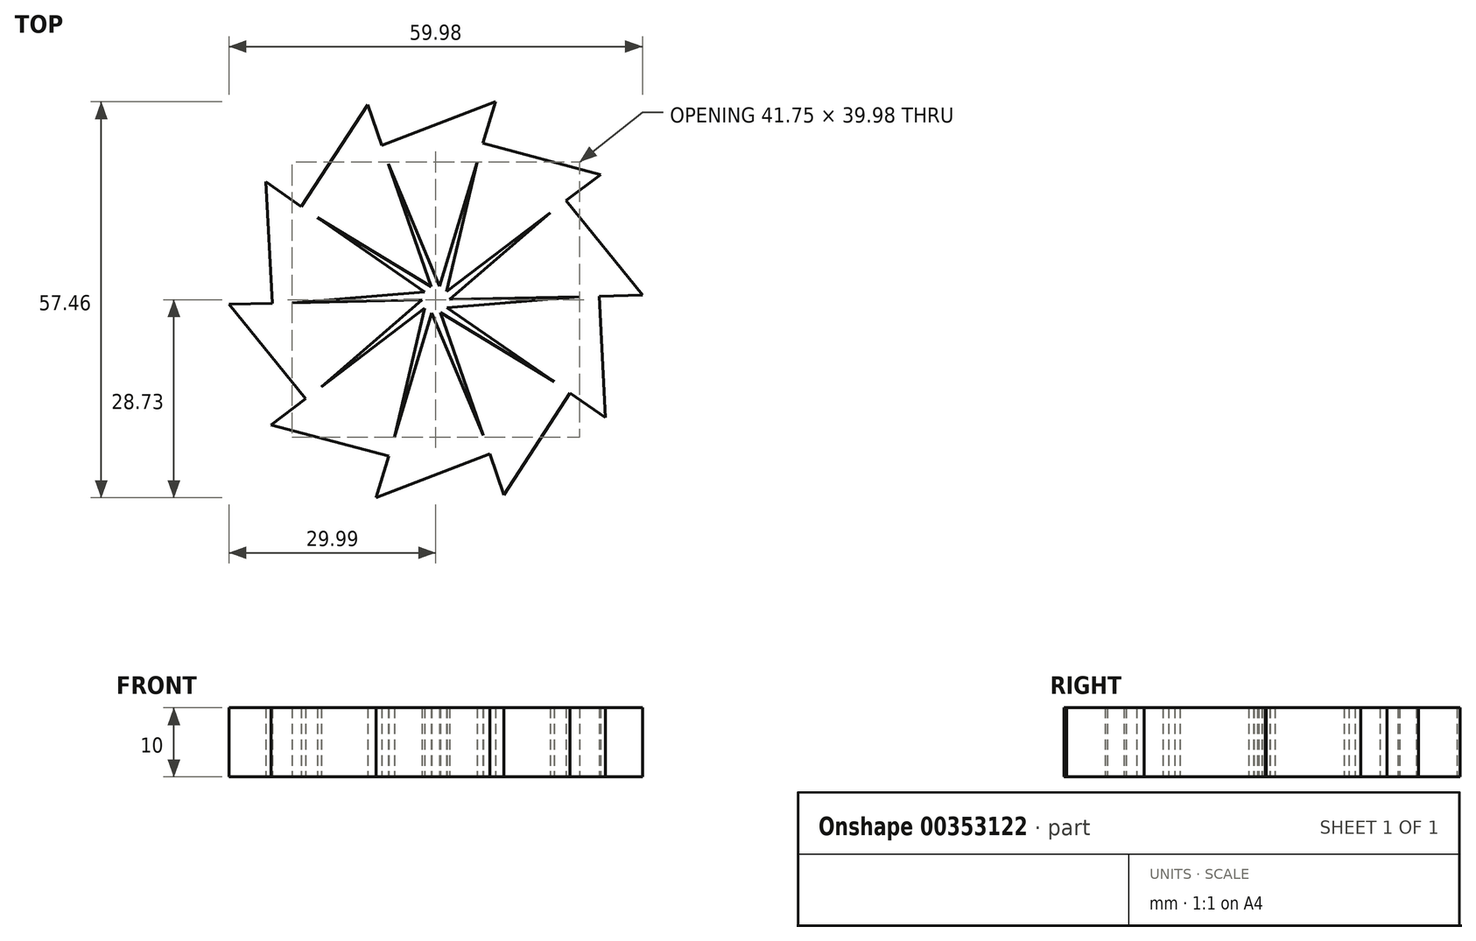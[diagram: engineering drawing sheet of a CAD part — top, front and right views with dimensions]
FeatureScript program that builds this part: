
annotation { "Feature Type Name" : "Feature", "Feature Type Description" : "" }
export const myFeature = defineFeature(function(context is Context, id is Id, definition is map)
    precondition{}
    {
        {
            var Q0;
            Q0=qCreatedBy(makeId("Top.planeOp"),FACE);
            var sketch = newSketch(context, id + "F0", { "sketchPlane" : qUnion([Q0])});
            skCircle(sketch, "E0", {"center": v(0, 0) * mm, "radius": 30 * mm, "construction": true});
            skCircle(sketch, "E1", {"center": v(0, 0) * mm, "radius": 23 * mm, "construction": true});
            skCircle(sketch, "E2", {"center": v(0, 0) * mm, "radius": 2 * mm, "construction": true});
            skSolve(sketch);
        }
        {
            var Q0;
            Q0=qCreatedBy(makeId("Top.planeOp"),FACE);
            var sketch = newSketch(context, id + "F1", { "sketchPlane" : qUnion([Q0])});
            skLineSegment(sketch, "E3", {"start": v(-30, -0.65) * mm, "end": v(-18.79, -14.5) * mm});
            skLineSegment(sketch, "E4", {"start": v(-18.23, -14.02) * mm, "end": v(-2, -0.04) * mm});
            skLineSegment(sketch, "E5", {"start": v(-30, -0.65) * mm, "end": v(-2, -0.04) * mm});
            skPoint(sketch, "E6.center", {"position": v(0, 0) * mm});
            skLineSegment(sketch, "E7.1.0", {"start": v(-23.88, -18.15) * mm, "end": v(-1.6, -1.21) * mm});
            skLineSegment(sketch, "E7.1.1", {"start": v(-23.88, -18.15) * mm, "end": v(-6.68, -22.77) * mm});
            skLineSegment(sketch, "E7.1.2", {"start": v(-6.5, -22.06) * mm, "end": v(-1.6, -1.21) * mm});
            skLineSegment(sketch, "E7.2.0", {"start": v(-8.65, -28.73) * mm, "end": v(-0.58, -1.92) * mm});
            skLineSegment(sketch, "E7.2.1", {"start": v(-8.65, -28.73) * mm, "end": v(7.98, -22.35) * mm});
            skLineSegment(sketch, "E7.2.2", {"start": v(7.7, -21.67) * mm, "end": v(-0.58, -1.92) * mm});
            skLineSegment(sketch, "E7.3.0", {"start": v(9.89, -28.32) * mm, "end": v(0.66, -1.89) * mm});
            skLineSegment(sketch, "E7.3.1", {"start": v(9.89, -28.32) * mm, "end": v(19.59, -13.4) * mm});
            skLineSegment(sketch, "E7.3.2", {"start": v(18.97, -13) * mm, "end": v(0.66, -1.89) * mm});
            skLineSegment(sketch, "E7.4.0", {"start": v(24.65, -17.1) * mm, "end": v(1.64, -1.14) * mm});
            skLineSegment(sketch, "E7.4.1", {"start": v(24.65, -17.1) * mm, "end": v(23.72, 0.68) * mm});
            skLineSegment(sketch, "E7.4.2", {"start": v(23, 0.63) * mm, "end": v(1.64, -1.14) * mm});
            skLineSegment(sketch, "E7.5.0", {"start": v(30, 0.65) * mm, "end": v(2, 0.04) * mm});
            skLineSegment(sketch, "E7.5.1", {"start": v(30, 0.65) * mm, "end": v(18.79, 14.5) * mm});
            skLineSegment(sketch, "E7.5.2", {"start": v(18.23, 14.02) * mm, "end": v(2, 0.04) * mm});
            skLineSegment(sketch, "E7.6.0", {"start": v(23.88, 18.15) * mm, "end": v(1.6, 1.21) * mm});
            skLineSegment(sketch, "E7.6.1", {"start": v(23.88, 18.15) * mm, "end": v(6.68, 22.77) * mm});
            skLineSegment(sketch, "E7.6.2", {"start": v(6.5, 22.06) * mm, "end": v(1.6, 1.21) * mm});
            skLineSegment(sketch, "E7.7.0", {"start": v(8.65, 28.73) * mm, "end": v(0.58, 1.92) * mm});
            skLineSegment(sketch, "E7.7.1", {"start": v(8.65, 28.73) * mm, "end": v(-7.98, 22.35) * mm});
            skLineSegment(sketch, "E7.7.2", {"start": v(-7.7, 21.67) * mm, "end": v(0.58, 1.92) * mm});
            skLineSegment(sketch, "E7.8.0", {"start": v(-9.89, 28.32) * mm, "end": v(-0.66, 1.89) * mm});
            skLineSegment(sketch, "E7.8.1", {"start": v(-9.89, 28.32) * mm, "end": v(-19.59, 13.4) * mm});
            skLineSegment(sketch, "E7.8.2", {"start": v(-18.97, 13) * mm, "end": v(-0.66, 1.89) * mm});
            skLineSegment(sketch, "E7.9.0", {"start": v(-24.65, 17.1) * mm, "end": v(-1.64, 1.14) * mm});
            skLineSegment(sketch, "E7.9.1", {"start": v(-24.65, 17.1) * mm, "end": v(-23.72, -0.68) * mm});
            skLineSegment(sketch, "E7.9.2", {"start": v(-23, -0.63) * mm, "end": v(-1.64, 1.14) * mm});
            skSolve(sketch);
        }
        {
            var Q0;
            {var subQ0=sQuery(id+"F1.wireOp",EDGE,"E5");var subQ3=sQuery(id+"F1.wireOp",EDGE,"E3");var subQ4=makeQuery(id+"F1.imprint","INTERSECT",VERTEX,{"derivedFrom":[subQ3,subQ0]});Q0=makeQuery(id+"F1.imprint","IMPRINT",FACE,{"disambiguationData":[TD([[makeQuery(id+"F1.imprint","IMPRINT",EDGE,{"disambiguationData":[TD([[subQ4,-1.0]])],"derivedFrom":subQ3}),1.0]])]});}
            var Q1;
            {var subQ4=sQuery(id+"F1.wireOp",EDGE,"E7.9.1");var subQ5=sQuery(id+"F1.wireOp",EDGE,"E5");var subQ6=makeQuery(id+"F1.imprint","INTERSECT",VERTEX,{"derivedFrom":[subQ5,subQ4]});Q1=makeQuery(id+"F1.imprint","IMPRINT",FACE,{"disambiguationData":[TD([[makeQuery(id+"F1.imprint","IMPRINT",EDGE,{"disambiguationData":[TD([[subQ6,-1.0]])],"derivedFrom":subQ5}),1.0]])]});}
            var Q2;
            {var subQ0=sQuery(id+"F1.wireOp",EDGE,"E7.8.1");var subQ1=sQuery(id+"F1.wireOp",EDGE,"E7.8.0");var subQ2=makeQuery(id+"F1.imprint","INTERSECT",VERTEX,{"derivedFrom":[subQ1,subQ0]});Q2=makeQuery(id+"F1.imprint","IMPRINT",FACE,{"disambiguationData":[TD([[makeQuery(id+"F1.imprint","IMPRINT",EDGE,{"disambiguationData":[TD([[subQ2,-1.0]])],"derivedFrom":subQ1}),-1.0]])]});}
            var Q3;
            {var subQ0=sQuery(id+"F1.wireOp",EDGE,"E7.7.1");var subQ1=sQuery(id+"F1.wireOp",EDGE,"E7.7.0");var subQ2=makeQuery(id+"F1.imprint","INTERSECT",VERTEX,{"derivedFrom":[subQ1,subQ0]});Q3=makeQuery(id+"F1.imprint","IMPRINT",FACE,{"disambiguationData":[TD([[makeQuery(id+"F1.imprint","IMPRINT",EDGE,{"disambiguationData":[TD([[subQ2,-1.0]])],"derivedFrom":subQ1}),-1.0]])]});}
            var Q4;
            {var subQ0=sQuery(id+"F1.wireOp",EDGE,"E7.6.1");var subQ1=sQuery(id+"F1.wireOp",EDGE,"E7.6.0");var subQ2=makeQuery(id+"F1.imprint","INTERSECT",VERTEX,{"derivedFrom":[subQ1,subQ0]});Q4=makeQuery(id+"F1.imprint","IMPRINT",FACE,{"disambiguationData":[TD([[makeQuery(id+"F1.imprint","IMPRINT",EDGE,{"disambiguationData":[TD([[subQ2,-1.0]])],"derivedFrom":subQ1}),-1.0]])]});}
            var Q5;
            {var subQ0=sQuery(id+"F1.wireOp",EDGE,"E7.5.1");var subQ1=sQuery(id+"F1.wireOp",EDGE,"E7.5.0");var subQ2=makeQuery(id+"F1.imprint","INTERSECT",VERTEX,{"derivedFrom":[subQ1,subQ0]});Q5=makeQuery(id+"F1.imprint","IMPRINT",FACE,{"disambiguationData":[TD([[makeQuery(id+"F1.imprint","IMPRINT",EDGE,{"disambiguationData":[TD([[subQ2,-1.0]])],"derivedFrom":subQ1}),-1.0]])]});}
            var Q6;
            {var subQ0=sQuery(id+"F1.wireOp",EDGE,"E7.4.1");var subQ1=sQuery(id+"F1.wireOp",EDGE,"E7.4.0");var subQ2=makeQuery(id+"F1.imprint","INTERSECT",VERTEX,{"derivedFrom":[subQ1,subQ0]});Q6=makeQuery(id+"F1.imprint","IMPRINT",FACE,{"disambiguationData":[TD([[makeQuery(id+"F1.imprint","IMPRINT",EDGE,{"disambiguationData":[TD([[subQ2,-1.0]])],"derivedFrom":subQ1}),-1.0]])]});}
            var Q7;
            {var subQ0=sQuery(id+"F1.wireOp",EDGE,"E7.3.1");var subQ1=sQuery(id+"F1.wireOp",EDGE,"E7.3.0");var subQ2=makeQuery(id+"F1.imprint","INTERSECT",VERTEX,{"derivedFrom":[subQ1,subQ0]});Q7=makeQuery(id+"F1.imprint","IMPRINT",FACE,{"disambiguationData":[TD([[makeQuery(id+"F1.imprint","IMPRINT",EDGE,{"disambiguationData":[TD([[subQ2,-1.0]])],"derivedFrom":subQ1}),-1.0]])]});}
            var Q8;
            {var subQ0=sQuery(id+"F1.wireOp",EDGE,"E7.2.1");var subQ1=sQuery(id+"F1.wireOp",EDGE,"E7.2.0");var subQ2=makeQuery(id+"F1.imprint","INTERSECT",VERTEX,{"derivedFrom":[subQ1,subQ0]});Q8=makeQuery(id+"F1.imprint","IMPRINT",FACE,{"disambiguationData":[TD([[makeQuery(id+"F1.imprint","IMPRINT",EDGE,{"disambiguationData":[TD([[subQ2,-1.0]])],"derivedFrom":subQ1}),-1.0]])]});}
            var Q9;
            {var subQ0=sQuery(id+"F1.wireOp",EDGE,"E7.1.1");var subQ1=sQuery(id+"F1.wireOp",EDGE,"E7.1.0");var subQ2=makeQuery(id+"F1.imprint","INTERSECT",VERTEX,{"derivedFrom":[subQ1,subQ0]});Q9=makeQuery(id+"F1.imprint","IMPRINT",FACE,{"disambiguationData":[TD([[makeQuery(id+"F1.imprint","IMPRINT",EDGE,{"disambiguationData":[TD([[subQ2,-1.0]])],"derivedFrom":subQ1}),-1.0]])]});}
            extrude(context, id + "F2", {"entities" : qUnion([Q0, Q1, Q2, Q3, Q4, Q5, Q6, Q7, Q8, Q9]), "depth" : 10 * mm});
        }
    });
